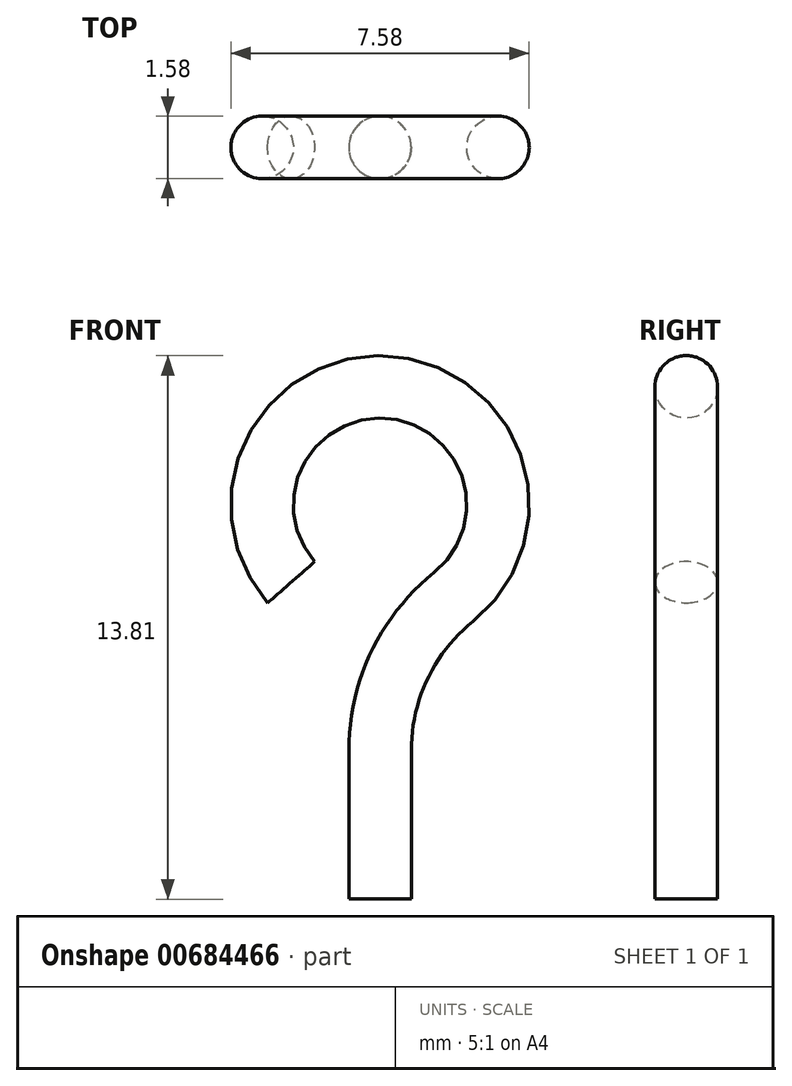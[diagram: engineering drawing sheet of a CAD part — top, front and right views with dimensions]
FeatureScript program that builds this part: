
annotation { "Feature Type Name" : "Feature", "Feature Type Description" : "" }
export const myFeature = defineFeature(function(context is Context, id is Id, definition is map)
    precondition{}
    {
        {
            var Q0;
            Q0=qCreatedBy(makeId("Front.planeOp"),FACE);
            var sketch = newSketch(context, id + "F0", { "sketchPlane" : qUnion([Q0])});
            skArc(sketch, "E0", {"start": v(1.87, -2.34) * mm, "mid": v(0.26, 2.99) * mm, "end": v(-2.25, -1.98) * mm});
            skLineSegment(sketch, "E1", {"start": v(0, 0) * mm, "end": v(-2.25, -1.98) * mm});
            skLineSegment(sketch, "E2", {"start": v(0, -6.24) * mm, "end": v(0, -10) * mm});
            skArc(sketch, "E3.filletArc", {"start": v(1.87, -2.34) * mm, "mid": v(0.5, -4.08) * mm, "end": v(0, -6.24) * mm});
            skSolve(sketch);
        }
        {
            var Q0;
            Q0=qCreatedBy(makeId("Top.planeOp"),FACE);
            cPlane(context, id + "F1", {"entities" : qUnion([Q0]), "cplaneType" : CPlaneType.OFFSET, "offset" : 10.02 * mm, "oppositeDirection" : true, "width" : 152.4 * mm, "height" : 152.4 * mm});
        }
        {
            var Q0;
            Q0=qCreatedBy(id+"F1.planeOp",FACE);
            var sketch = newSketch(context, id + "F2", { "sketchPlane" : qUnion([Q0])});
            skCircle(sketch, "E4", {"center": v(0, 0) * mm, "radius": 0.8 * mm});
            skSolve(sketch);
        }
        {
            var Q0;
            Q0=makeQuery(id+"F2.imprint","IMPRINT",FACE,{"disambiguationData":[TD([[makeQuery(id+"F2.imprint","IMPRINT",EDGE,{"derivedFrom":sQuery(id+"F2.wireOp",EDGE,"E4")}),1.0]])]});
            var Q1;
            Q1=sQuery(id+"F0.wireOp",EDGE,"E2");
            var Q2;
            Q2=sQuery(id+"F0.wireOp",EDGE,"E3.filletArc");
            var Q3;
            Q3=sQuery(id+"F0.wireOp",EDGE,"E0");
            sweep(context, id + "F3", {"profiles" : qUnion([Q0]), "path" : qUnion([Q1, Q2, Q3])});
        }
    });
